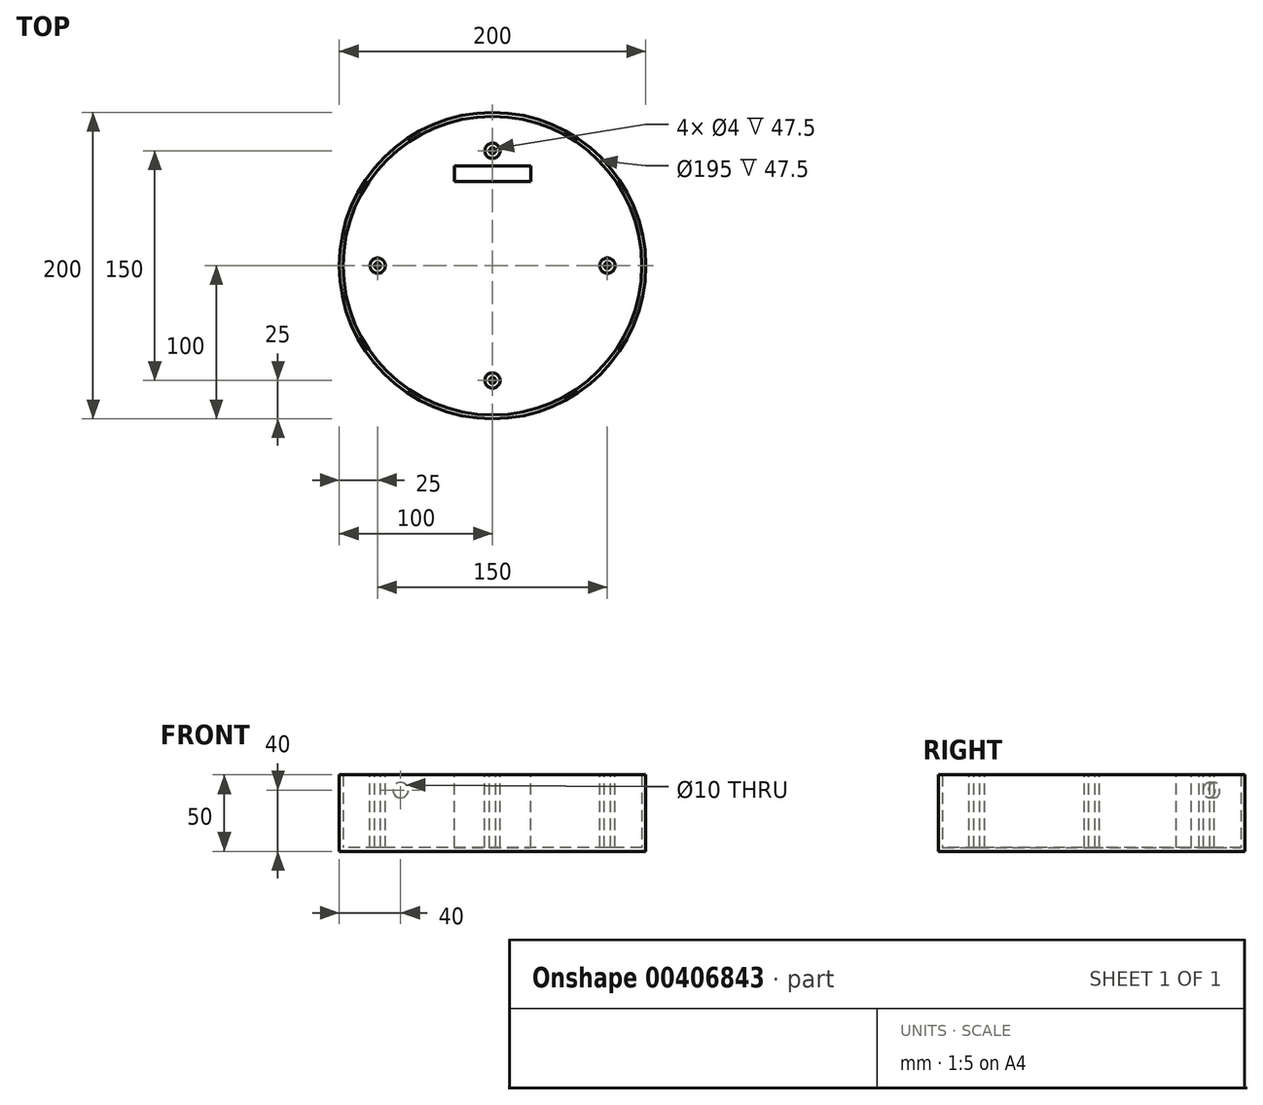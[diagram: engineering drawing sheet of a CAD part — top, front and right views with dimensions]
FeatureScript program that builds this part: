
annotation { "Feature Type Name" : "Feature", "Feature Type Description" : "" }
export const myFeature = defineFeature(function(context is Context, id is Id, definition is map)
    precondition{}
    {
        {
            var Q0;
            Q0=qCreatedBy(makeId("Top.planeOp"),FACE);
            var sketch = newSketch(context, id + "F0", { "sketchPlane" : qUnion([Q0])});
            skCircle(sketch, "E0", {"center": v(0, 0) * mm, "radius": 100 * mm});
            skSolve(sketch);
        }
        {
            var Q0;
            Q0 = qSketchRegion(id + "F0", true);
            extrude(context, id + "F1", {"entities" : qUnion([Q0]), "depth" : 50 * mm});
        }
        {
            var Q0;
            Q0=makeQuery(id+"F1.opExtrude","CAP_FACE",FACE,{"disambiguationData":[OSD([sQuery(id+"F0.wireOp",EDGE,"E0")])],"isStart":false});
            shell(context, id + "F2", {"entities" : qUnion([Q0]), "thickness" : 2.5 * mm});
        }
        {
            var Q0;
            Q0=makeQuery(id+"F1.opExtrude","CAP_FACE",FACE,{"disambiguationData":[OSD([sQuery(id+"F0.wireOp",EDGE,"E0")])],"isStart":false});
            var sketch = newSketch(context, id + "F3", { "sketchPlane" : qUnion([Q0])});
            skCircle(sketch, "E1", {"center": v(-75, 0) * mm, "radius": 5 * mm});
            skCircle(sketch, "E2", {"center": v(-75, 0) * mm, "radius": 2 * mm});
            skCircle(sketch, "E3.1.0", {"center": v(0, -75) * mm, "radius": 5 * mm});
            skCircle(sketch, "E3.1.1", {"center": v(0, -75) * mm, "radius": 2 * mm});
            skCircle(sketch, "E3.2.0", {"center": v(75, 0) * mm, "radius": 5 * mm});
            skCircle(sketch, "E3.2.1", {"center": v(75, 0) * mm, "radius": 2 * mm});
            skCircle(sketch, "E3.3.0", {"center": v(0, 75) * mm, "radius": 5 * mm});
            skCircle(sketch, "E3.3.1", {"center": v(0, 75) * mm, "radius": 2 * mm});
            skPoint(sketch, "E3.center", {"position": v(0, 0) * mm});
            skSolve(sketch);
        }
        {
            var Q0;
            Q0 = qSketchRegion(id + "F3", true);
            extrude(context, id + "F4", {"entities" : qUnion([Q0]), "operationType" : NewBodyOperationType.ADD, "endBound" : BoundingType.UP_TO_NEXT, "oppositeDirection" : true, "depth" : 25 * mm});
        }
        {
            var Q0;
            Q0=makeQuery(id+"F1.opExtrude","CAP_FACE",FACE,{"disambiguationData":[OSD([sQuery(id+"F0.wireOp",EDGE,"E0")])],"isStart":false});
            var sketch = newSketch(context, id + "F5", { "sketchPlane" : qUnion([Q0])});
            skLineSegment(sketch, "E4.bottom", {"start": v(25, 55) * mm, "end": v(-25, 55) * mm});
            skLineSegment(sketch, "E4.top", {"start": v(25, 65) * mm, "end": v(-25, 65) * mm});
            skLineSegment(sketch, "E4.left", {"start": v(25, 55) * mm, "end": v(25, 65) * mm});
            skLineSegment(sketch, "E4.right", {"start": v(-25, 55) * mm, "end": v(-25, 65) * mm});
            skPoint(sketch, "E4.middle", {"position": v(0, 60) * mm});
            skSolve(sketch);
        }
        {
            var Q0;
            Q0=qCreatedBy(makeId("Front.planeOp"),FACE);
            var sketch = newSketch(context, id + "F6", { "sketchPlane" : qUnion([Q0])});
            skCircle(sketch, "E5", {"center": v(-60, 40) * mm, "radius": 5 * mm});
            skSolve(sketch);
        }
        {
            var Q0;
            Q0 = qSketchRegion(id + "F6", true);
            extrude(context, id + "F7", {"entities" : qUnion([Q0]), "operationType" : NewBodyOperationType.REMOVE, "endBound" : BoundingType.THROUGH_ALL, "oppositeDirection" : true, "depth" : 25 * mm});
        }
        {
            var Q0;
            Q0 = qSketchRegion(id + "F5", true);
            extrude(context, id + "F8", {"entities" : qUnion([Q0]), "operationType" : NewBodyOperationType.ADD, "endBound" : BoundingType.UP_TO_NEXT, "oppositeDirection" : true, "depth" : 25 * mm});
        }
    });
